# Revit family: Skylight-Wasco-Low_Profile
name_source: partatom
category: Windows
revit_build: Autodesk Revit Architecture 2013 (Build: 20130531_2115(x64)
units: mm (PartAtom-declared; Revit-internal decimal feet)

## types (18) — shared parameters
Curb = Rubber, Black
Curb Height = 0' - 4"
Curb Mount = Yes
Curb Width = 0' - 2"
Deck Mount = No
Default Elevation = 0' - 0"
Description = Skylight
Finish = Aluminum - Wasco - Aged Copper
Glazing 1 1_16 = No
Glazing 1 3_16 = No
Glazing 1 5_16 = Yes
Glazing Material = Glass - Wasco - Clear
Height = 0' - 3 5/8"
Host Constraint = 1
Manufacturer = Wasco
Product Documentation Link = http://www.wascoskylights.com
Product Name = Low Profile
Product Page URL = http://www.wascoskylights.com
Rough Height = 0' - 7 5/8"
URL = http://www.wascoskylights.com

## per-type parameters (varying)
| type | 1' 4" Rafter Spacing | 2' Rafter Spacing | Host Length | Host Width | Length | Model | Rafter Array | Rough Length | Rough Width | Width |
| LPGS/LPG-2448 (2' Rafter Spacing) | No | Yes | 4' - 1 1/2" | 6' - 1 1/2" | 2' - 1 1/2" | LPGS-2448 | 1 | 1' - 10 1/2" | 3' - 10 1/2" | 4' - 1 1/2" |
| LPGS/LPG-2472 (2' Rafter Spacing) | No | Yes | 4' - 1 1/2" | 8' - 1 1/2" | 2' - 1 1/2" | LPGS-2472 | 1 | 1' - 10 1/2" | 5' - 10 1/2" | 6' - 1 1/2" |
| LPGS/LPG-4848 (2' Rafter Spacing) | No | Yes | 6' - 1 1/2" | 6' - 1 1/2" | 4' - 1 1/2" | LPGS-4848 | 1 | 3' - 10 1/2" | 3' - 10 1/2" | 4' - 1 1/2" |
| LPGS/LPG-4872 (2' Rafter Spacing) | No | Yes | 6' - 1 1/2" | 8' - 1 1/2" | 4' - 1 1/2" | LPGS-4872 | 1 | 3' - 10 1/2" | 5' - 10 1/2" | 6' - 1 1/2" |
| LPGS/LPG-7248 (2' Rafter Spacing) | No | Yes | 8' - 1 1/2" | 6' - 1 1/2" | 6' - 1 1/2" | LPGS-7248 | 2 | 5' - 10 1/2" | 3' - 10 1/2" | 4' - 1 1/2" |
| LPGS/LPG-7272 (2' Rafter Spacing) | No | Yes | 8' - 1 1/2" | 8' - 1 1/2" | 6' - 1 1/2" | LPGS-7272 | 2 | 5' - 10 1/2" | 5' - 10 1/2" | 6' - 1 1/2" |
| LPGS/LPG-9648 (2' Rafter Spacing) | No | Yes | 10' - 1 1/2" | 6' - 1 1/2" | 8' - 1 1/2" | LPGS-9648 | 3 | 7' - 10 1/2" | 3' - 10 1/2" | 4' - 1 1/2" |
| LPGS/LPG-9672 (2' Rafter Spacing) | No | Yes | 10' - 1 1/2" | 8' - 1 1/2" | 8' - 1 1/2" | LPGS-9672 | 3 | 7' - 10 1/2" | 5' - 10 1/2" | 6' - 1 1/2" |
| LPGS/LPG-12048 (2' Rafter Spacing) | No | Yes | 12' - 1 1/2" | 6' - 1 1/2" | 10' - 1 1/2" | LPGS-12048 | 4 | 9' - 10 1/2" | 3' - 10 1/2" | 4' - 1 1/2" |
| LPGS/LPG-12072 (2' Rafter Spacing) | No | Yes | 12' - 1 1/2" | 8' - 1 1/2" | 10' - 1 1/2" | LPGS-12072 | 4 | 9' - 10 1/2" | 5' - 10 1/2" | 6' - 1 1/2" |
| LPGS/LPG-3248 (1' 4" Rafter Spacing) | Yes | No | 4' - 9 1/2" | 6' - 1 1/2" | 2' - 9 1/2" | LPGS-3248 | 1 | 2' - 6 1/2" | 3' - 10 1/2" | 4' - 1 1/2" |
| LPGS/LPG-3272 (1' 4" Rafter Spacing) | Yes | No | 4' - 9 1/2" | 8' - 1 1/2" | 2' - 9 1/2" | LPGS-3272 | 1 | 2' - 6 1/2" | 5' - 10 1/2" | 6' - 1 1/2" |
| LPGS/LPG-6448 (1' 4" Rafter Spacing) | Yes | No | 7' - 5 1/2" | 6' - 1 1/2" | 5' - 5 1/2" | LPGS-6448 | 1 | 5' - 2 1/2" | 3' - 10 1/2" | 4' - 1 1/2" |
| LPGS/LPG-6472 (1' 4" Rafter Spacing) | Yes | No | 7' - 5 1/2" | 8' - 1 1/2" | 5' - 5 1/2" | LPGS-6472 | 1 | 5' - 2 1/2" | 5' - 10 1/2" | 6' - 1 1/2" |
| LPGS/LPG-9648 (1' 4" Rafter Spacing) | Yes | No | 10' - 1 1/2" | 6' - 1 1/2" | 8' - 1 1/2" | LPGS-9648 | 2 | 7' - 10 1/2" | 3' - 10 1/2" | 4' - 1 1/2" |
| LPGS/LPG-9672 (1' 4" Rafter Spacing) | Yes | No | 10' - 1 1/2" | 8' - 1 1/2" | 8' - 1 1/2" | LPGS-9672 | 2 | 7' - 10 1/2" | 5' - 10 1/2" | 6' - 1 1/2" |
| LPGS/LPG-12848 (1' 4" Rafter Spacing) | Yes | No | 12' - 9 1/2" | 6' - 1 1/2" | 10' - 9 1/2" | LPGS-12848 | 3 | 10' - 6 1/2" | 3' - 10 1/2" | 4' - 1 1/2" |
| LPGS/LPG-12872 (1' 4" Rafter Spacing) | Yes | No | 12' - 9 1/2" | 8' - 1 1/2" | 10' - 9 1/2" | LPGS-12872 | 3 | 10' - 6 1/2" | 5' - 10 1/2" | 6' - 1 1/2" |

## geometry (parser evidence)
native form markers: Blend x16, Sweep x19
no freeform markers — native parametric forms only
